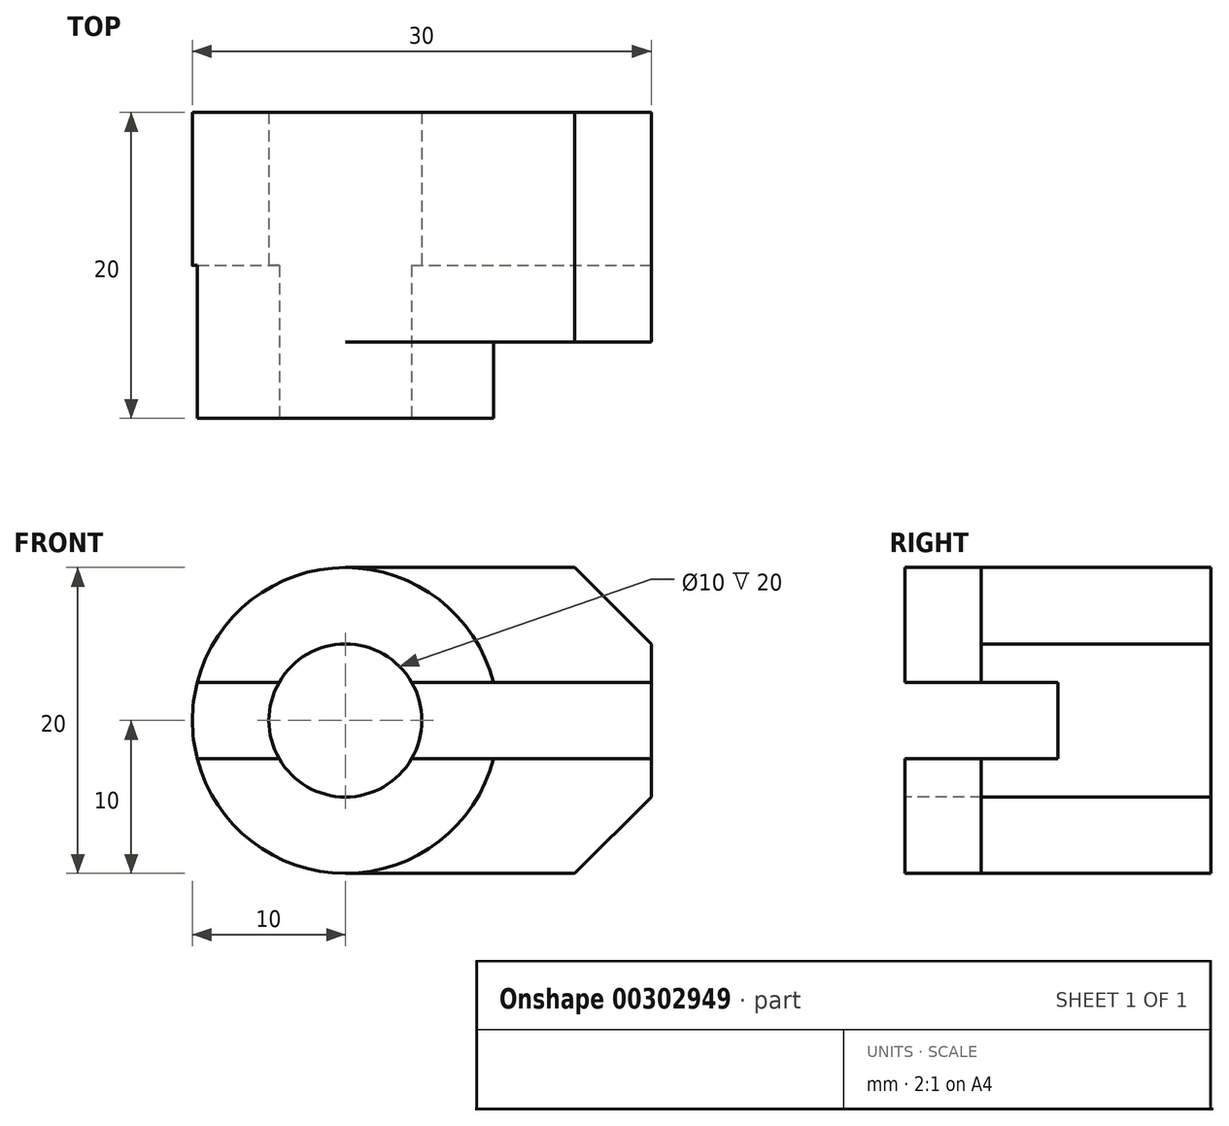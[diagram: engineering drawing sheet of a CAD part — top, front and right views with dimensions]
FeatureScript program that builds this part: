
annotation { "Feature Type Name" : "Feature", "Feature Type Description" : "" }
export const myFeature = defineFeature(function(context is Context, id is Id, definition is map)
    precondition{}
    {
        {
            var Q0;
            Q0=qCreatedBy(makeId("Front.planeOp"),FACE);
            var sketch = newSketch(context, id + "F0", { "sketchPlane" : qUnion([Q0])});
            skCircle(sketch, "E0", {"center": v(0, 0) * mm, "radius": 10 * mm});
            skLineSegment(sketch, "E1", {"start": v(0, 10) * mm, "end": v(15, 10) * mm});
            skLineSegment(sketch, "E2", {"start": v(0, -10) * mm, "end": v(15, -10) * mm});
            skLineSegment(sketch, "E3", {"start": v(15, -10) * mm, "end": v(20, -10) * mm});
            skLineSegment(sketch, "E4", {"start": v(20, -10) * mm, "end": v(20, -5) * mm});
            skLineSegment(sketch, "E5", {"start": v(20, -5) * mm, "end": v(15, -10) * mm});
            skLineSegment(sketch, "E6", {"start": v(20, -5) * mm, "end": v(20, 5) * mm});
            skLineSegment(sketch, "E7", {"start": v(20, 5) * mm, "end": v(15, 10) * mm});
            skSolve(sketch);
        }
        {
            var Q0;
            {var subQ0=sQuery(id+"F0.wireOp",EDGE,"E0");var subQ1=makeQuery(id+"F0.imprint","INTERSECT",VERTEX,{"derivedFrom":[subQ0,sQuery(id+"F0.wireOp",EDGE,"E1")]});Q0=makeQuery(id+"F0.imprint","IMPRINT",FACE,{"disambiguationData":[TD([[makeQuery(id+"F0.imprint","IMPRINT",EDGE,{"disambiguationData":[TD([[subQ1,-1.0]])],"derivedFrom":subQ0}),1.0]])]});}
            var Q1;
            {var subQ1=sQuery(id+"F0.wireOp",EDGE,"E1");Q1=makeQuery(id+"F0.imprint","IMPRINT",FACE,{"disambiguationData":[TD([[makeQuery(id+"F0.imprint","IMPRINT",EDGE,{"derivedFrom":subQ1}),-1.0]])]});}
            extrude(context, id + "F1", {"entities" : qUnion([Q0, Q1]), "depth" : 20 * mm});
        }
        {
            var Q0;
            Q0=makeQuery(id+"F1.opExtrude","SWEPT_FACE",FACE,{"disambiguationData":[OSD([sQuery(id+"F0.wireOp",EDGE,"E6")])]});
            var sketch = newSketch(context, id + "F2", { "sketchPlane" : qUnion([Q0])});
            skLineSegment(sketch, "E8", {"start": v(-20, 0) * mm, "end": v(-20, 2.5) * mm});
            skLineSegment(sketch, "E9", {"start": v(-20, 2.5) * mm, "end": v(-10, 2.5) * mm});
            skLineSegment(sketch, "E10", {"start": v(-10, 2.5) * mm, "end": v(-10, -2.5) * mm});
            skLineSegment(sketch, "E11", {"start": v(-10, -2.5) * mm, "end": v(-20, -2.5) * mm});
            skLineSegment(sketch, "E12", {"start": v(-20, -2.5) * mm, "end": v(-20, 0) * mm});
            skSolve(sketch);
        }
        {
            var Q0;
            Q0=makeQuery(id+"F2.imprint","IMPRINT",FACE,{"disambiguationData":[TD([[makeQuery(id+"F2.imprint","IMPRINT",EDGE,{"derivedFrom":sQuery(id+"F2.wireOp",EDGE,"E8")}),-1.0]])]});
            extrude(context, id + "F3", {"entities" : qUnion([Q0]), "operationType" : NewBodyOperationType.REMOVE, "oppositeDirection" : true, "depth" : 50 * mm});
        }
        {
            var Q0;
            {var subQ0=sQuery(id+"F0.wireOp",EDGE,"E7");var subQ1=sQuery(id+"F0.wireOp",EDGE,"E6");var subQ2=sQuery(id+"F0.wireOp",EDGE,"E1");var subQ3=sQuery(id+"F0.wireOp",EDGE,"E0");Q0=makeQuery(id+"F3.boolean.opBoolean","SPLIT",FACE,{"disambiguationData":[TD([makeQuery(id+"F1.opExtrude","SWEPT_FACE",FACE,{"disambiguationData":[OSD([subQ2])]})])],"derivedFrom":makeQuery(id+"F1.opExtrude","CAP_FACE",FACE,{"disambiguationData":[OSD([subQ3,subQ2,sQuery(id+"F0.wireOp",EDGE,"E2"),sQuery(id+"F0.wireOp",EDGE,"E5"),subQ1,subQ0])],"isStart":false})});}
            var sketch = newSketch(context, id + "F4", { "sketchPlane" : qUnion([Q0])});
            skArc(sketch, "E13.0.0", {"start": v(0, 10) * mm, "mid": v(-6.12, 7.9) * mm, "end": v(-9.68, 2.5) * mm});
            skLineSegment(sketch, "E13.0.1", {"start": v(-9.68, 2.5) * mm, "end": v(20, 2.5) * mm});
            skLineSegment(sketch, "E13.0.2", {"start": v(20, 2.5) * mm, "end": v(20, 5) * mm});
            skLineSegment(sketch, "E13.0.3", {"start": v(20, 5) * mm, "end": v(15, 10) * mm});
            skLineSegment(sketch, "E13.0.4", {"start": v(15, 10) * mm, "end": v(0, 10) * mm});
            skLineSegment(sketch, "E14.0.0", {"start": v(20, -2.5) * mm, "end": v(-9.68, -2.5) * mm});
            skArc(sketch, "E14.0.1", {"start": v(-9.68, -2.5) * mm, "mid": v(-6.12, -7.9) * mm, "end": v(0, -10) * mm});
            skLineSegment(sketch, "E14.0.2", {"start": v(0, -10) * mm, "end": v(15, -10) * mm});
            skLineSegment(sketch, "E14.0.3", {"start": v(15, -10) * mm, "end": v(20, -5) * mm});
            skLineSegment(sketch, "E14.0.4", {"start": v(20, -5) * mm, "end": v(20, -2.5) * mm});
            skCircle(sketch, "E15", {"center": v(0, 0) * mm, "radius": 5 * mm});
            skCircle(sketch, "E16", {"center": v(0, 0) * mm, "radius": 10 * mm});
            skSolve(sketch);
        }
        {
            var Q0;
            {var subQ1=sQuery(id+"F4.wireOp",EDGE,"E14.0.2");Q0=makeQuery(id+"F4.imprint","IMPRINT",FACE,{"disambiguationData":[TD([[makeQuery(id+"F4.imprint","IMPRINT",EDGE,{"derivedFrom":subQ1}),1.0]])]});}
            var Q1;
            {var subQ1=sQuery(id+"F4.wireOp",EDGE,"E13.0.2");Q1=makeQuery(id+"F4.imprint","IMPRINT",FACE,{"disambiguationData":[TD([[makeQuery(id+"F4.imprint","IMPRINT",EDGE,{"derivedFrom":subQ1}),1.0]])]});}
            extrude(context, id + "F5", {"entities" : qUnion([Q0, Q1]), "operationType" : NewBodyOperationType.REMOVE, "oppositeDirection" : true, "depth" : 5 * mm});
        }
        {
            var Q0;
            {var subQ0=sQuery(id+"F0.wireOp",EDGE,"E7");var subQ1=sQuery(id+"F0.wireOp",EDGE,"E6");var subQ2=sQuery(id+"F0.wireOp",EDGE,"E1");var subQ3=sQuery(id+"F0.wireOp",EDGE,"E0");Q0=makeQuery(id+"F3.boolean.opBoolean","SPLIT",FACE,{"disambiguationData":[TD([makeQuery(id+"F1.opExtrude","SWEPT_FACE",FACE,{"disambiguationData":[OSD([subQ2])]})])],"derivedFrom":makeQuery(id+"F1.opExtrude","CAP_FACE",FACE,{"disambiguationData":[OSD([subQ3,subQ2,sQuery(id+"F0.wireOp",EDGE,"E2"),sQuery(id+"F0.wireOp",EDGE,"E5"),subQ1,subQ0])],"isStart":false})});}
            var sketch = newSketch(context, id + "F6", { "sketchPlane" : qUnion([Q0])});
            skCircle(sketch, "E17", {"center": v(0, 0) * mm, "radius": 5 * mm});
            skSolve(sketch);
        }
        {
            var Q0;
            {var subQ0=sQuery(id+"F6.wireOp",EDGE,"E17");var subQ1=makeQuery(id+"F3.boolean.opBoolean","COPY",EDGE,{"derivedFrom":makeQuery(id+"F3.opExtrude","SWEPT_EDGE",EDGE,{"disambiguationData":[OSD([sQuery(id+"F0.wireOp",EDGE,"E6"),sQuery(id+"F2.wireOp",EDGE,"E8"),sQuery(id+"F2.wireOp",EDGE,"E9")])]})});var subQ2=makeQuery(id+"F6.imprint","INTERSECT",VERTEX,{"disambiguationData":[OD(0.0)],"derivedFrom":[subQ1,subQ0]});Q0=makeQuery(id+"F6.imprint","IMPRINT",FACE,{"disambiguationData":[TD([[makeQuery(id+"F6.imprint","IMPRINT",EDGE,{"disambiguationData":[TD([[subQ2,-1.0]])],"derivedFrom":subQ0}),1.0]])]});}
            var Q1;
            {var subQ0=sQuery(id+"F6.wireOp",EDGE,"E17");var subQ1=makeQuery(id+"F3.boolean.opBoolean","COPY",EDGE,{"derivedFrom":makeQuery(id+"F3.opExtrude","SWEPT_EDGE",EDGE,{"disambiguationData":[OSD([sQuery(id+"F0.wireOp",EDGE,"E6"),sQuery(id+"F2.wireOp",EDGE,"E8"),sQuery(id+"F2.wireOp",EDGE,"E9")])]})});var subQ2=makeQuery(id+"F6.imprint","INTERSECT",VERTEX,{"disambiguationData":[OD(0.0)],"derivedFrom":[subQ1,subQ0]});Q1=makeQuery(id+"F6.imprint","IMPRINT",FACE,{"disambiguationData":[TD([[makeQuery(id+"F6.imprint","IMPRINT",EDGE,{"disambiguationData":[TD([[subQ2,1.0]])],"derivedFrom":subQ0}),1.0]])]});}
            extrude(context, id + "F7", {"entities" : qUnion([Q0, Q1]), "operationType" : NewBodyOperationType.REMOVE, "oppositeDirection" : true, "depth" : 25 * mm});
        }
    });
